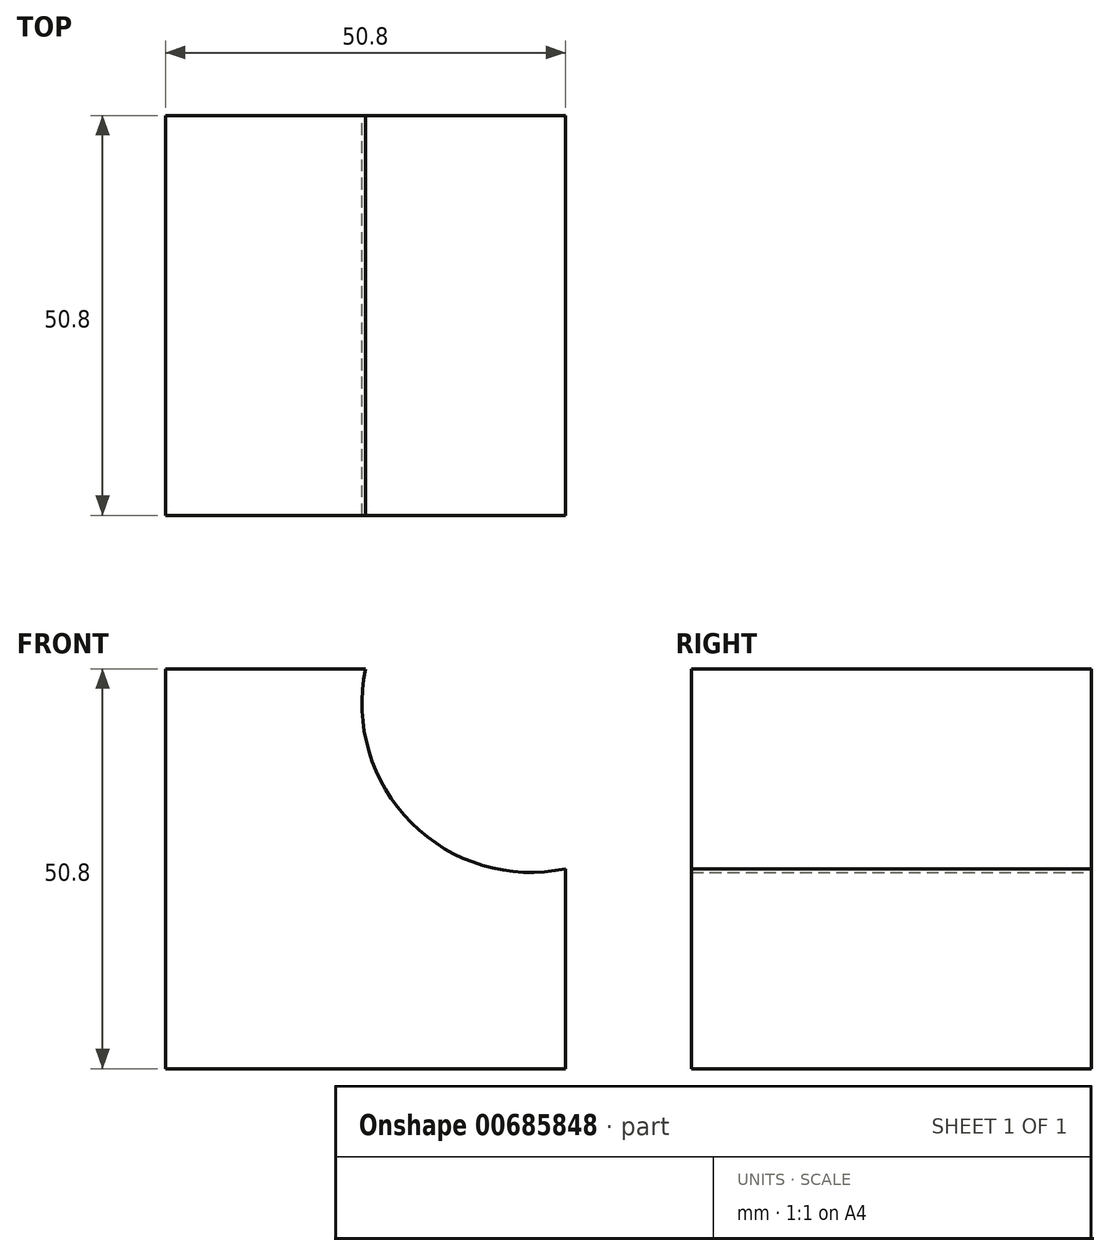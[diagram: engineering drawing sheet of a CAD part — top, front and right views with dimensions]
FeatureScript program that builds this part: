
annotation { "Feature Type Name" : "Feature", "Feature Type Description" : "" }
export const myFeature = defineFeature(function(context is Context, id is Id, definition is map)
    precondition{}
    {
        {
            var Q0;
            Q0=qCreatedBy(makeId("Front.planeOp"),FACE);
            var sketch = newSketch(context, id + "F0", { "sketchPlane" : qUnion([Q0])});
            skLineSegment(sketch, "E0", {"start": v(0, 0) * mm, "end": v(-50.8, 0) * mm});
            skLineSegment(sketch, "E1", {"start": v(-50.8, 0) * mm, "end": v(-50.8, 50.8) * mm});
            skLineSegment(sketch, "E2", {"start": v(-50.8, 50.8) * mm, "end": v(-25.4, 50.8) * mm});
            skLineSegment(sketch, "E3", {"start": v(0, 0) * mm, "end": v(0, 25.4) * mm});
            skArc(sketch, "E4", {"start": v(-25.4, 50.8) * mm, "mid": v(-19.58, 31.22) * mm, "end": v(0, 25.4) * mm});
            skSolve(sketch);
        }
        {
            var Q0;
            Q0 = qSketchRegion(id + "F0", true);
            extrude(context, id + "F1", {"entities" : qUnion([Q0]), "depth" : 50.8 * mm, "offsetDistance" : 25.4 * mm});
        }
    });
